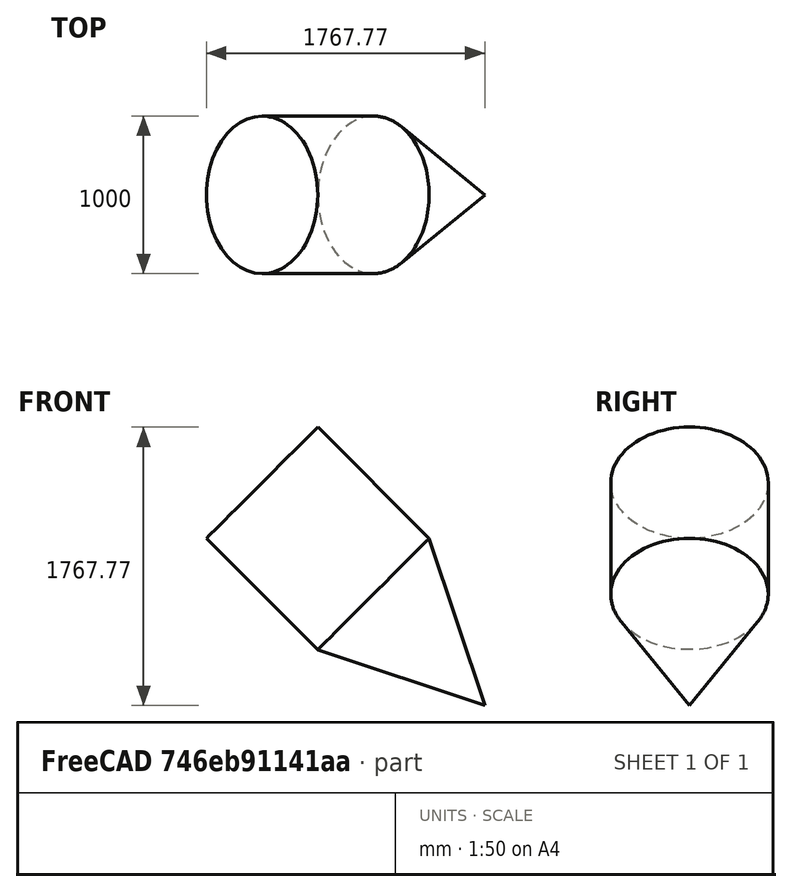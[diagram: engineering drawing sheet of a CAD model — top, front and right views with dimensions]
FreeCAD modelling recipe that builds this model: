
FCSTD DOCUMENT  (FreeCAD 1.0R39319 (Git))
Label: test_module
License: Creative Commons Attribution 4.0
LicenseURL: https://creativecommons.org/licenses/by/4.0/
objects: Sketcher::SketchObject×1, PartDesign::Line×1, PartDesign::Revolution×1, PartDesign::Body×1
note: 7 computed .brp shape members not serialized (recipe doc carries the construction recipe); baked Part::Feature solids carry a one-line shape summary decoded from their .brp

FEATURE [Sketcher::SketchObject] Sketch
  ArcFitTolerance = 1e-06
  AttachmentSupport = -> [XZ_Plane]
  FullyConstrained = true
  MakeInternals = false
  MapMode = 5
  Placement = pos=(0,0,0) rot=(1,0,0;1.5708rad)
  sketch-geometry (5):
    g0: LineSegment StartX=-486.107 StartY=486.107 StartZ=0 EndX=-132.553 EndY=839.66 EndZ=0
    g1: LineSegment StartX=-132.553 StartY=839.66 StartZ=0 EndX=574.553 EndY=132.553 EndZ=0
    g2: LineSegment StartX=574.553 StartY=132.553 StartZ=0 EndX=928.107 EndY=-928.107 EndZ=0
    g3: LineSegment StartX=928.107 StartY=-928.107 StartZ=0 EndX=-486.107 EndY=486.107 EndZ=0
    g4: LineSegment [constr] StartX=574.553 StartY=132.553 StartZ=0 EndX=221 EndY=-221 EndZ=0
  constraints (15):
    c: Coincident(g0,g1)
    c: Coincident(g1,g2)
    c: Coincident(g3,g0)
    c: Coincident(g3,g2)
    c: Perpendicular(g0,g1)
    c: Perpendicular(g3,g0)
    c: Distance(g3,g3) = 2000
    c: Distance(g0,g0) = 500
    c: Distance(g1,g1) = 1000
    c: Angle(g3,g-1) = 0.785398
    c: PointOnObject(g-1,g3)
    c: Coincident(g4,g1)
    c: Symmetric(g3,g3,g4)
    c: Distance(g4,g-2) = 221
    c: DistanceY(g4,g-1) = 221
FEATURE [PartDesign::Line] DatumLine
  AttacherType = Attacher::AttachEngineLine
  AttachmentOffset = pos=(0,0,0) rot=(1,0,0;0.785398rad)
  AttachmentSupport = -> [X_Axis]
  Length = 20
  MapMode = 29
  Placement = pos=(0,0,0) rot=(0.678598,0.678598,0.281085;2.59356rad)
  ResizeMode = 0
FEATURE [PartDesign::Revolution] Revolution
  Angle = 360
  Angle2 = 60
  Axis = (0.707107,0,-0.707107)
  Base = (0,0,0)
  Placement = pos=(0,0,0) rot=(1,0,0;1.5708rad)
  Profile = -> Sketch
  ReferenceAxis = -> DatumLine
  Reversed = true
  Suppressed = false
  Type = 0
FEATURE [PartDesign::Body] Body
  AllowCompound = false
  Group = -> [DatumLine,Sketch,Revolution]
  Origin = -> Origin
  Tip = -> Revolution
